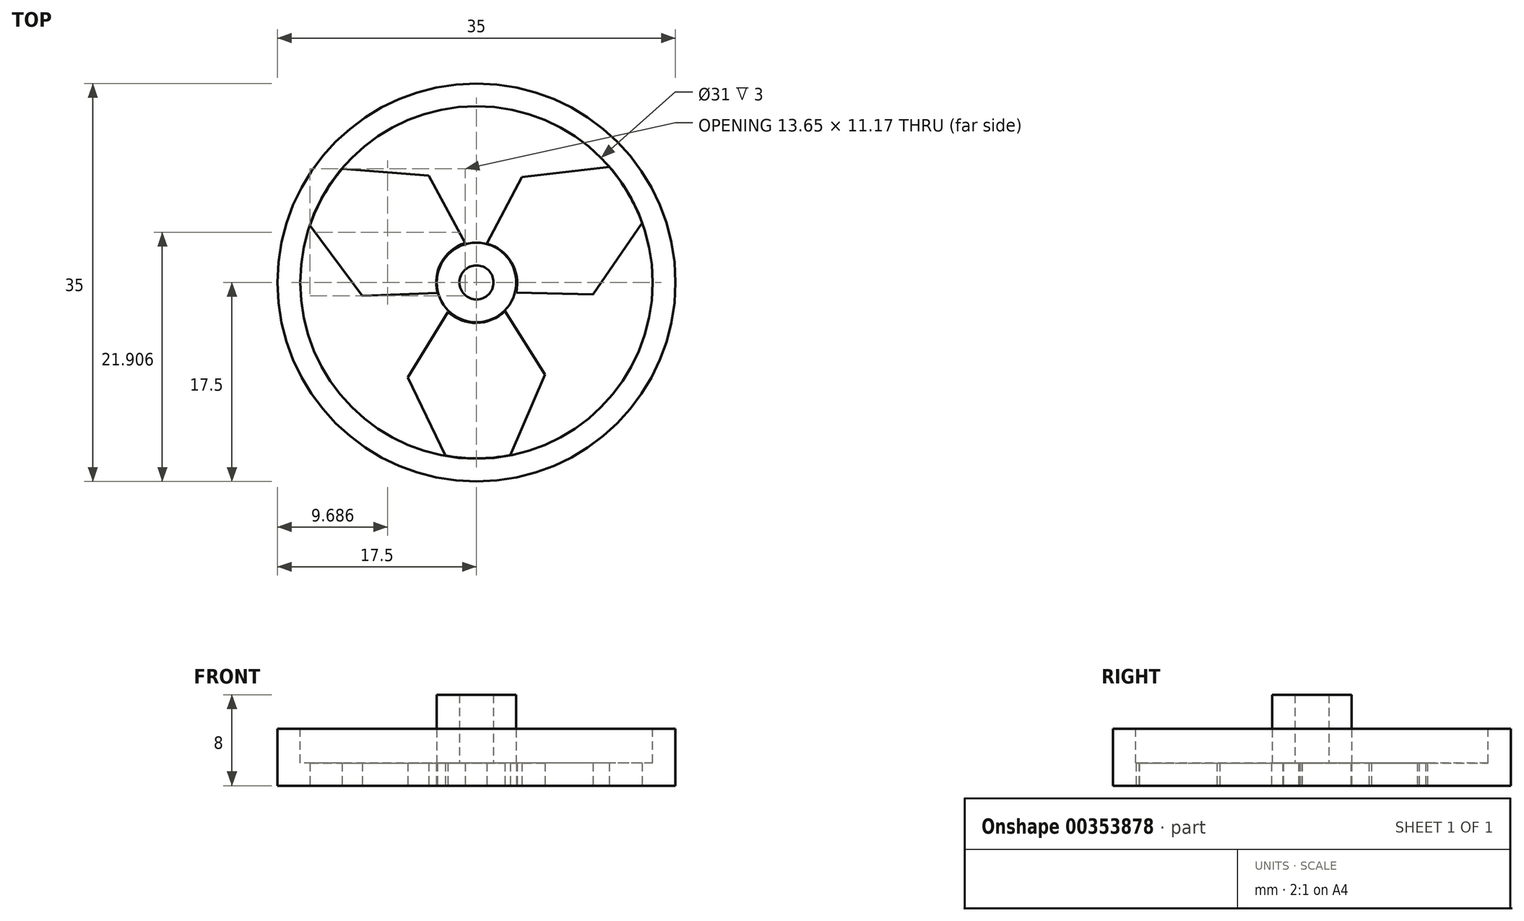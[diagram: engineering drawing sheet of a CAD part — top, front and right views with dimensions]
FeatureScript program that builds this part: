
annotation { "Feature Type Name" : "Feature", "Feature Type Description" : "" }
export const myFeature = defineFeature(function(context is Context, id is Id, definition is map)
    precondition{}
    {
        {
            var Q0;
            Q0=qCreatedBy(makeId("Top.planeOp"),FACE);
            var sketch = newSketch(context, id + "F0", { "sketchPlane" : qUnion([Q0])});
            skCircle(sketch, "E0", {"center": v(0, 0) * mm, "radius": 17.5 * mm});
            skSolve(sketch);
        }
        {
            var Q0;
            Q0 = qSketchRegion(id + "F0", true);
            extrude(context, id + "F1", {"entities" : qUnion([Q0]), "depth" : 5 * mm});
        }
        {
            var Q0;
            Q0=makeQuery(id+"F1.opExtrude","CAP_FACE",FACE,{"disambiguationData":[OSD([sQuery(id+"F0.wireOp",EDGE,"E0")])],"isStart":false});
            var sketch = newSketch(context, id + "F2", { "sketchPlane" : qUnion([Q0])});
            skCircle(sketch, "E1", {"center": v(0, 0) * mm, "radius": 15.5 * mm});
            skSolve(sketch);
        }
        {
            var Q0;
            Q0 = qSketchRegion(id + "F2", true);
            extrude(context, id + "F3", {"entities" : qUnion([Q0]), "operationType" : NewBodyOperationType.REMOVE, "oppositeDirection" : true, "depth" : 3 * mm});
        }
        {
            var Q0;
            Q0=makeQuery(id+"F3.boolean.opBoolean","COPY",FACE,{"derivedFrom":makeQuery(id+"F3.opExtrude","CAP_FACE",FACE,{"disambiguationData":[OSD([sQuery(id+"F2.wireOp",EDGE,"E1")])],"isStart":false})});
            var sketch = newSketch(context, id + "F4", { "sketchPlane" : qUnion([Q0])});
            skCircle(sketch, "E2", {"center": v(0, 0) * mm, "radius": 1.5 * mm});
            skCircle(sketch, "E3", {"center": v(0, 0) * mm, "radius": 3.5 * mm});
            skSolve(sketch);
        }
        {
            var Q0;
            Q0 = qSketchRegion(id + "F4", true);
            extrude(context, id + "F5", {"entities" : qUnion([Q0]), "operationType" : NewBodyOperationType.ADD, "depth" : 6 * mm});
        }
        {
            var Q0;
            Q0=makeQuery(id+"F1.opExtrude","CAP_FACE",FACE,{"disambiguationData":[OSD([sQuery(id+"F0.wireOp",EDGE,"E0")])],"isStart":true});
            var sketch = newSketch(context, id + "F6", { "sketchPlane" : qUnion([Q0])});
            skCircle(sketch, "E4", {"center": v(0, 0) * mm, "radius": 3.5 * mm});
            skCircle(sketch, "E5", {"center": v(0, 0) * mm, "radius": 15.5 * mm});
            skSolve(sketch);
        }
        {
            var Q0;
            Q0=makeQuery(id+"F6.imprint","IMPRINT",FACE,{"disambiguationData":[TD([[makeQuery(id+"F6.imprint","IMPRINT",EDGE,{"derivedFrom":sQuery(id+"F6.wireOp",EDGE,"E4")}),-1.0]])]});
            var sketch = newSketch(context, id + "F7", { "sketchPlane" : qUnion([Q0])});
            skLineSegment(sketch, "E6", {"start": v(2.5, 2.51) * mm, "end": v(6.04, 8.1) * mm});
            skLineSegment(sketch, "E7", {"start": v(6.04, 8.1) * mm, "end": v(2.97, 15.19) * mm});
            skLineSegment(sketch, "E8", {"start": v(-2.51, 2.6) * mm, "end": v(-6.04, 8.35) * mm});
            skLineSegment(sketch, "E9", {"start": v(-6.04, 8.35) * mm, "end": v(-2.74, 15.23) * mm});
            skArc(sketch, "E10", {"start": v(2.5, 2.51) * mm, "mid": v(0.01, 3.55) * mm, "end": v(-2.51, 2.6) * mm});
            skArc(sketch, "E11", {"start": v(2.97, 15.19) * mm, "mid": v(0.12, 15.47) * mm, "end": v(-2.74, 15.23) * mm});
            skLineSegment(sketch, "E12.1.0", {"start": v(-10.03, 1.18) * mm, "end": v(-14.64, -5.02) * mm});
            skArc(sketch, "E12.1.1", {"start": v(-14.64, -5.02) * mm, "mid": v(-13.46, -7.64) * mm, "end": v(-11.81, -9.99) * mm});
            skLineSegment(sketch, "E12.1.2", {"start": v(-4.2, -9.4) * mm, "end": v(-11.81, -9.99) * mm});
            skLineSegment(sketch, "E12.1.3", {"start": v(-1, -3.47) * mm, "end": v(-4.2, -9.4) * mm});
            skArc(sketch, "E12.1.4", {"start": v(-3.43, 0.91) * mm, "mid": v(-3.08, -1.77) * mm, "end": v(-1, -3.47) * mm});
            skLineSegment(sketch, "E12.1.5", {"start": v(-3.43, 0.91) * mm, "end": v(-10.03, 1.18) * mm});
            skLineSegment(sketch, "E12.2.0", {"start": v(4, -9.28) * mm, "end": v(11.66, -10.17) * mm});
            skArc(sketch, "E12.2.1", {"start": v(11.66, -10.17) * mm, "mid": v(13.34, -7.84) * mm, "end": v(14.56, -5.24) * mm});
            skLineSegment(sketch, "E12.2.2", {"start": v(10.25, 1.06) * mm, "end": v(14.56, -5.24) * mm});
            skLineSegment(sketch, "E12.2.3", {"start": v(3.5, 0.88) * mm, "end": v(10.25, 1.06) * mm});
            skArc(sketch, "E12.2.4", {"start": v(0.92, -3.42) * mm, "mid": v(3.07, -1.79) * mm, "end": v(3.5, 0.88) * mm});
            skLineSegment(sketch, "E12.2.5", {"start": v(0.92, -3.42) * mm, "end": v(4, -9.28) * mm});
            skPoint(sketch, "E12.center", {"position": v(0, 0) * mm});
            skSolve(sketch);
        }
        {
            var Q0;
            Q0 = qSketchRegion(id + "F7", true);
            extrude(context, id + "F8", {"entities" : qUnion([Q0]), "operationType" : NewBodyOperationType.REMOVE, "oppositeDirection" : true, "depth" : 25 * mm});
        }
    });
